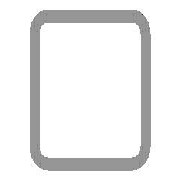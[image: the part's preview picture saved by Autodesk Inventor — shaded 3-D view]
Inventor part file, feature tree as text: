
AUTODESK INVENTOR PART (.ipt)
format: ipt  version: 2025 (Build 290162010, 162A)  size: 133,632 bytes
history: native  units: mm (DEFAULTED — no unit token found)
features: other x4, sketch x1, plane x1
ambient origin geometry x8: Origin, YZ Plane, XZ Plane, XY Plane, X Axis, Y Axis, Z Axis, Center Point
bodies: Solid1 (feature_tree), Body (feature_tree)
feature tree (6):
  parser-record x1  (decoder bookkeeping rows leaked as tree rows — omitted from the tree; the rows remain in map.json)
  other  "Driven Length"
  other  "Start Plane"
  other  "End Plane"
  sketch  "Sketch3"  dims[d3=535.0mm d4=0.0mm d7=6.0mm d9=50.0mm d11=50.0mm d12=3.0mm d13=20.0mm d14=555.0mm d15=25.0mm d16=25.0mm d17=90.0deg d18=535.0mm]
  plane  "Work Plane3"
